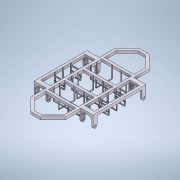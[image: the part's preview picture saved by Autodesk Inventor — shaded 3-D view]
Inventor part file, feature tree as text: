
AUTODESK INVENTOR PART (.ipt)
format: ipt  version: 2020 (Build 240168000, 168)  size: 1,189,888 bytes
history: native  units: mm
features: extrude x23, sketch x22, shell x1, fillet x1
ambient origin geometry x8: Origin, YZ Plane, XZ Plane, XY Plane, X Axis, Y Axis, Z Axis, Center Point
bodies: Volumenkörper1 (feature_tree)
feature tree (47):
  extrude  "Extrusion1"  Depth=1060.0mm
  extrude  "Extrusion2"  Depth=50.0mm
  extrude  "Extrusion3"  Depth=1160.0mm
  extrude  "Extrusion5"  Depth=250.0mm
  shell  "Wandung3"  Thickness=90.0deg
  extrude  "Extrusion9"  Depth=50.0mm
  extrude  "Extrusion10"  Depth=50.0mm TaperAngle=0.0deg
  fillet  "Rundung3"  Radius=320.0mm
  extrude  "Extrusion11"  Depth=320.0mm
  extrude  "Extrusion12"  Depth=320.0mm
  extrude  "Extrusion13"  Depth=240.0mm
  extrude  "Extrusion14"  Depth=40.0mm
  extrude  "Extrusion15"  Depth=485.0mm
  extrude  "Extrusion16"  Depth=50.0mm TaperAngle=0.0deg
  extrude  "Extrusion17"  Depth=500.0mm
  extrude  "Extrusion18"  Depth=250.0mm
  extrude  "Extrusion20"  Depth=50.0mm
  extrude  "Extrusion21"  Depth=50.0mm
  extrude  "Extrusion22"  Depth=50.0mm
  extrude  "Extrusion23"  Depth=80.0mm
  extrude  "Extrusion24"  Depth=200.0mm TaperAngle=0.0deg
  extrude  "Extrusion25"  Depth=40.0mm
  extrude  "Extrusion26"  Depth=200.0mm
  extrude  "Extrusion27"  Depth=100.0mm
  extrude  "Extrusion28"  Depth=10.0mm
  sketch  "Skizze1"  dims[d0=590.0mm d1=1060.0mm]
  sketch  "Skizze3"  dims[d3=50.0mm d4=50.0mm]
  sketch  "Skizze5"  dims[d5=690.0mm d6=1160.0mm]
  sketch  "Skizze6"  dims[d7=50.0mm d8=0.0mm d13=250.0mm d14=90.0deg]
  sketch  "Skizze10"  dims[d28=135.0deg d32=50.0mm]
  sketch  "Skizze11"  dims[d33=220.711mm d35=50.0mm d36=0.0mm d38=320.0mm]
  sketch  "Skizze12"  dims[d39=50.0mm d40=320.0mm]
  sketch  "Skizze13"  dims[d41=50.0mm d42=320.0mm]
  sketch  "Skizze14"  dims[d45=485.0mm d51=240.0mm]
  sketch  "Skizze15"  dims[d52=40.0mm d53=40.0mm]
  sketch  "Skizze16"  dims[d54=50.0mm d55=0.0mm d62=485.0mm]
  sketch  "Skizze17"  dims[d69=50.0mm d70=50.0mm d71=0.0mm]
  sketch  "Skizze18"  dims[d77=5.0mm d81=500.0mm]
  sketch  "Skizze20"  dims[d82=90.0deg d83=250.0mm]
  sketch  "Skizze21"  dims[d84=135.0deg d87=50.0mm]
  sketch  "Skizze22"  dims[d88=50.0mm d89=50.0mm]
  sketch  "Skizze23"  dims[d91=90.0deg d92=50.0mm]
  sketch  "Skizze24"  dims[d93=25.0mm d94=80.0mm]
  sketch  "Skizze25"  dims[d96=180.0deg d101=200.0mm d102=0.0mm]
  sketch  "Skizze26"  dims[d109=1500.0mm d110=0.0mm d111=40.0mm]
  sketch  "Skizze27"  dims[d112=200.0mm d115=200.0mm]
  sketch  "Skizze28"  dims[d116=100.0mm d117=100.0mm d118=10.0mm d119=10.0mm d120=10.0mm d121=10.0mm d122=5.0mm d123=20.0mm d124=5.0mm d125=20.0mm d126=20.0mm d127=5.0mm d128=20.0mm d129=5.0mm d130=190.0mm d131=190.0mm d132=90.0mm d133=90.0mm d134=5.0mm d135=20.0mm d136=5.0mm d137=20.0mm d138=20.0mm d139=5.0mm d140=20.0mm d141=5.0mm d142=25.0mm d143=590.0mm d144=90.0deg d145=240.0mm d146=0.0mm d147=5.0mm d148=5.0mm d149=2000.0mm d150=0.0mm d151=5.0mm d152=0.0mm d153=5.0mm d154=0.0mm d155=210.0mm d156=25.0mm d157=40.0mm d158=40.0mm d159=40.0mm d160=275.0mm d161=90.0deg d162=5.0mm d163=20.0mm d164=140.0mm d165=90.0deg d166=5.0mm d167=20.0mm d168=140.0mm d169=5.0mm d170=20.0mm d171=90.0deg d172=210.0mm d173=0.0mm d174=5.0mm d175=0.0mm d176=50.0mm d177=20.0mm d178=190.0mm d179=20.0mm d180=5.0mm d181=0.0mm d182=5.0mm d183=20.0mm d184=5.0mm d185=20.0mm d186=5.0mm d187=5.0mm d188=20.0mm d189=25.0mm d190=0.0mm d197=190.0mm d198=20.0mm d199=55.0mm d200=190.0mm d201=20.0mm d202=5.0mm d203=0.0mm d204=5.0mm d205=20.0mm d206=5.0mm d207=20.0mm d208=5.0mm d209=20.0mm d210=5.0mm d211=20.0mm d212=25.0mm d213=0.0mm d214=40.0mm d215=40.0mm d216=40.0mm d217=275.0mm d218=90.0deg d219=20.0mm d220=140.0mm d221=20.0mm d222=180.0deg d223=140.0mm d224=180.0deg d225=20.0mm d226=5.0mm d227=20.0mm d228=5.0mm d229=20.0mm d230=5.0mm d231=20.0mm d232=210.0mm d233=0.0mm d234=5.0mm d235=0.0mm d236=190.0mm d237=20.0mm d238=50.0mm d239=90.0deg d240=5.0mm d241=20.0mm d242=185.0mm d243=20.0mm d244=5.0mm d245=0.0mm d246=5.0mm d247=20.0mm d248=5.0mm d249=20.0mm d250=5.0mm d251=20.0mm d252=5.0mm d253=20.0mm d254=25.0mm d255=0.0mm d256=190.0mm d257=20.0mm d258=55.0mm d259=90.0deg d260=190.0mm d261=20.0mm d262=5.0mm d263=0.0mm d264=5.0mm d265=20.0mm d266=5.0mm d267=20.0mm d268=5.0mm d269=20.0mm d270=5.0mm d271=20.0mm d272=25.0mm d273=0.0mm d274=50.0mm d275=45.0deg d276=50.0mm d277=180.0deg d278=45.0deg d279=50.0mm d280=90.0deg d281=315.0deg d282=50.0mm d283=0.0mm d284=45.0deg d285=80.0mm d286=0.0mm]
